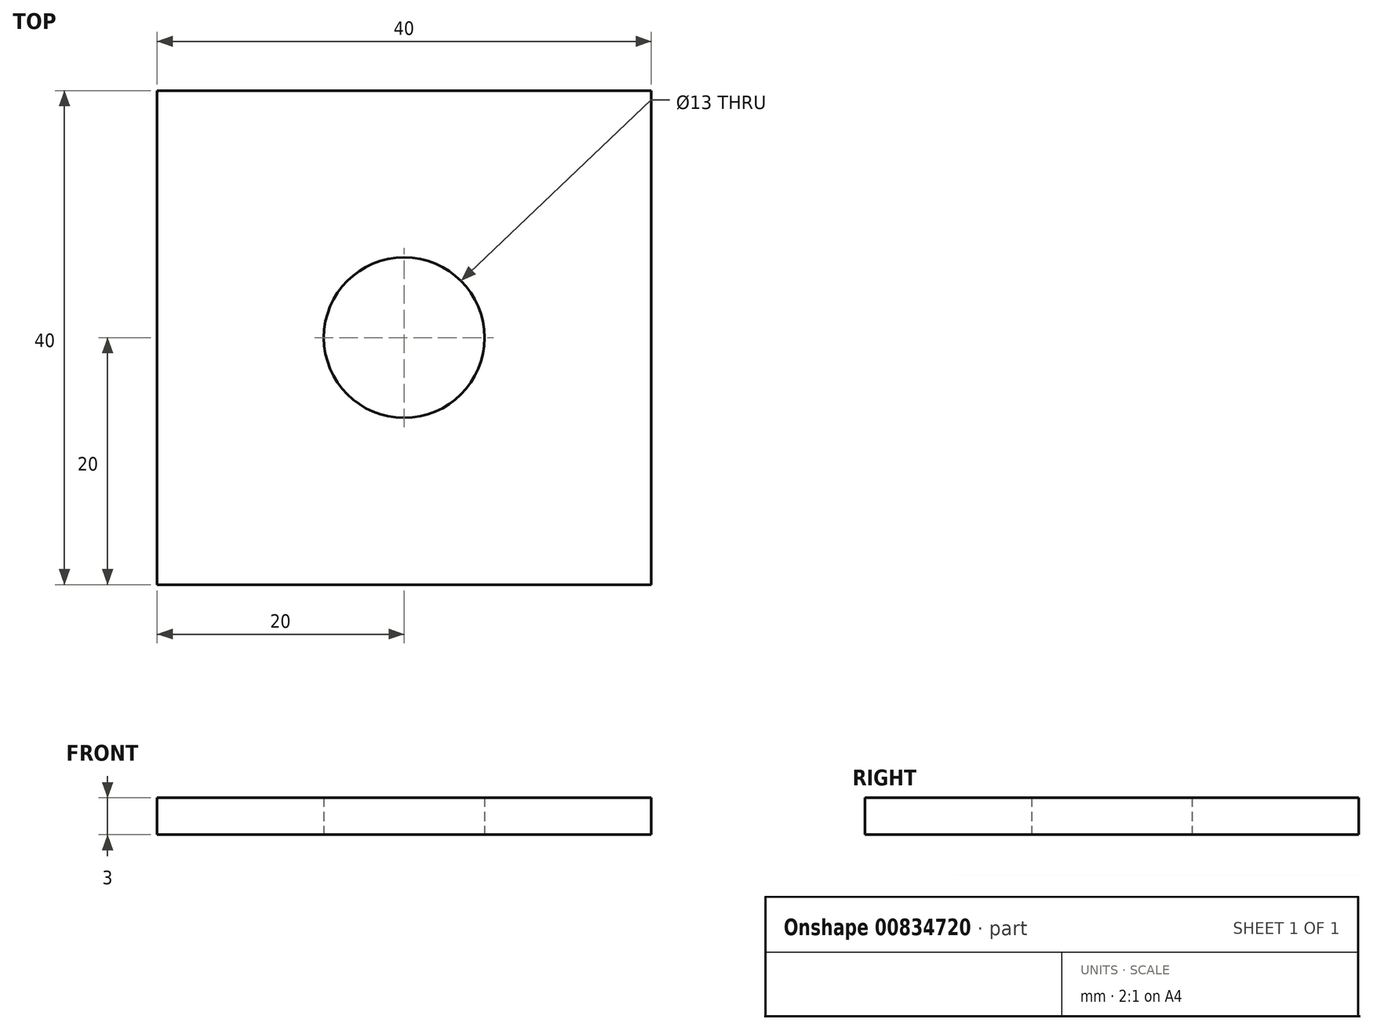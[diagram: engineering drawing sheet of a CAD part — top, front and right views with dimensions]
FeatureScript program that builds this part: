
annotation { "Feature Type Name" : "Feature", "Feature Type Description" : "" }
export const myFeature = defineFeature(function(context is Context, id is Id, definition is map)
    precondition{}
    {
        {
            var Q0;
            Q0=qCreatedBy(makeId("Top.planeOp"),FACE);
            var sketch = newSketch(context, id + "F0", { "sketchPlane" : qUnion([Q0])});
            skCircle(sketch, "E0", {"center": v(0, 0) * mm, "radius": 6.5 * mm});
            skLineSegment(sketch, "E1.bottom", {"start": v(-20, 20) * mm, "end": v(20, 20) * mm});
            skLineSegment(sketch, "E1.top", {"start": v(-20, -20) * mm, "end": v(20, -20) * mm});
            skLineSegment(sketch, "E1.left", {"start": v(-20, 20) * mm, "end": v(-20, -20) * mm});
            skLineSegment(sketch, "E1.right", {"start": v(20, 20) * mm, "end": v(20, -20) * mm});
            skSolve(sketch);
        }
        {
            var Q0;
            Q0=makeQuery(id+"F0.imprint","IMPRINT",FACE,{"disambiguationData":[TD([[makeQuery(id+"F0.imprint","IMPRINT",EDGE,{"derivedFrom":sQuery(id+"F0.wireOp",EDGE,"E0")}),-1.0]])]});
            extrude(context, id + "F1", {"entities" : qUnion([Q0]), "depth" : 3 * mm, "offsetDistance" : 25 * mm});
        }
    });
